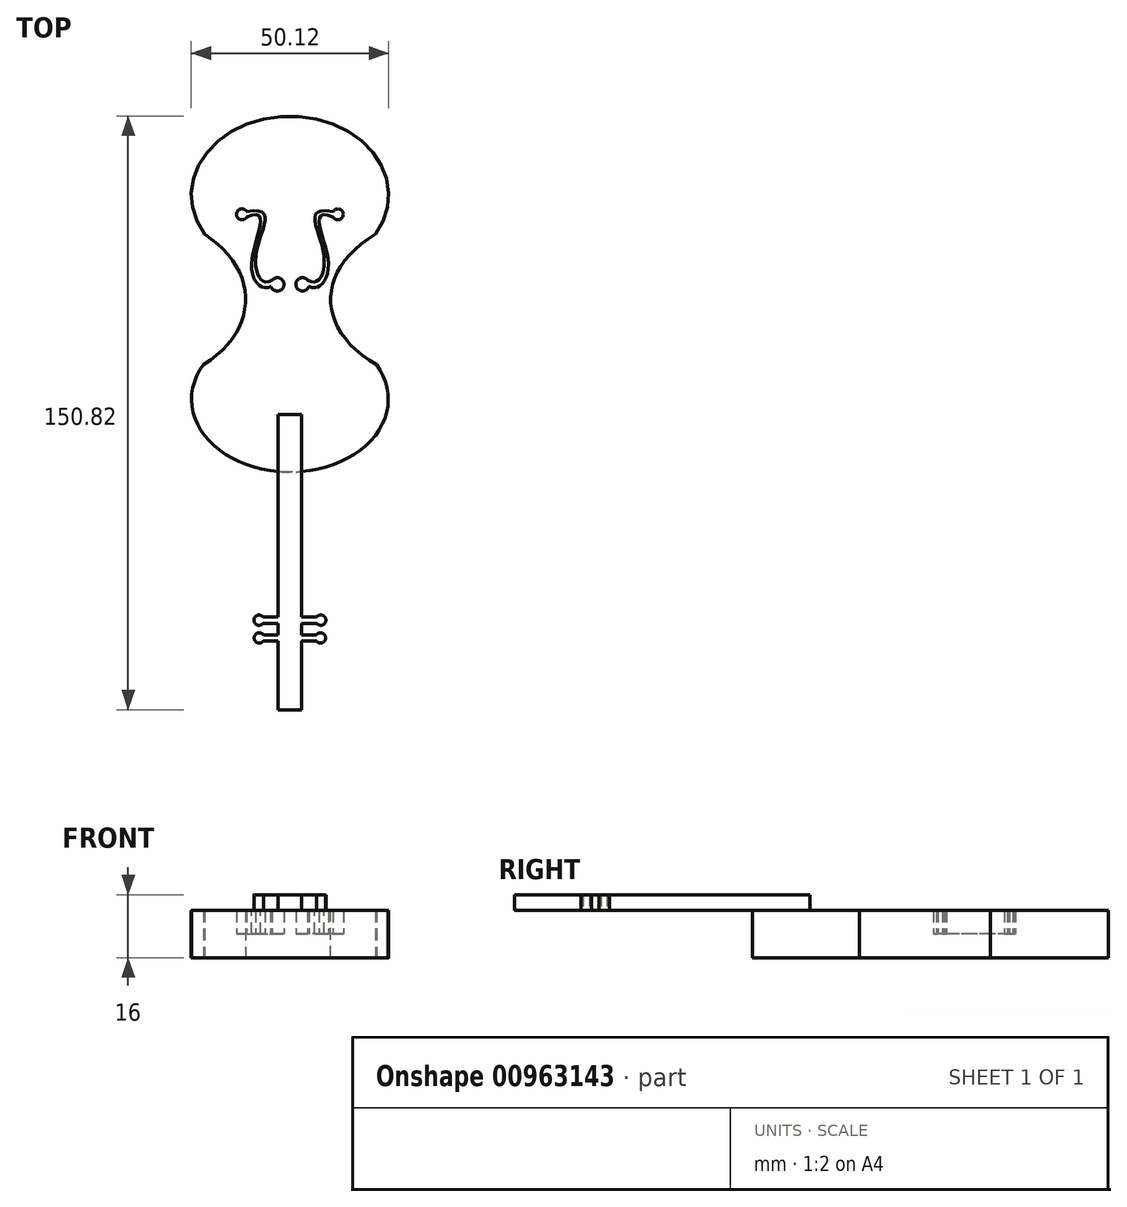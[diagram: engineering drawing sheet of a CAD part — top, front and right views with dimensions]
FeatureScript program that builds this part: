
annotation { "Feature Type Name" : "Feature", "Feature Type Description" : "" }
export const myFeature = defineFeature(function(context is Context, id is Id, definition is map)
    precondition{}
    {
        {
            var Q0;
            Q0=qCreatedBy(makeId("Top.planeOp"),FACE);
            var sketch = newSketch(context, id + "F0", { "sketchPlane" : qUnion([Q0])});
            skEllipticalArc(sketch, "E0", {});
            skEllipticalArc(sketch, "E1", {});
            skFitSpline(sketch, "E2", {"points": [v(21.74, 18.23) * mm, v(21.98, -14.95) * mm], "startDerivative": vector(-46.01, -28.19) * mm, "endDerivative": vector(46.18, -27.1) * mm});
            skFitSpline(sketch, "E3", {"points": [v(-21.74, 18.23) * mm, v(-21.98, -14.95) * mm], "startDerivative": vector(42.04, -27.25) * mm, "endDerivative": vector(-42.74, -26.33) * mm});
            const initialGuessF0  = {"E0": [0, -0.023745077083508568, 1, 0, 0.024989771066984055, 0.018479709246510986, 2.6455513247437614, 0.49604132884603214], "E1": [0, 0.02818056562631233, 1, 0, 0.025062327598065877, 0.020010533803968472, 5.762777835649319, 3.662000125120059]};
            skSetInitialGuess(sketch, initialGuessF0);
            skSolve(sketch);
        }
        {
            var Q0;
            Q0=makeQuery(id+"F0.imprint","IMPRINT",FACE,{"disambiguationData":[TD([[makeQuery(id+"F0.imprint","IMPRINT",EDGE,{"derivedFrom":sQuery(id+"F0.wireOp",EDGE,"E0")}),1.0]])]});
            extrude(context, id + "F1", {"entities" : qUnion([Q0]), "depth" : 6 * mm, "offsetDistance" : 25 * mm});
        }
        {
            var Q0;
            Q0=makeQuery(id+"F1.opExtrude","CAP_FACE",FACE,{"disambiguationData":[OSD([sQuery(id+"F0.wireOp",EDGE,"E0"),sQuery(id+"F0.wireOp",EDGE,"E1"),sQuery(id+"F0.wireOp",EDGE,"E2"),sQuery(id+"F0.wireOp",EDGE,"E3")])],"isStart":false});
            var sketch = newSketch(context, id + "F2", { "sketchPlane" : qUnion([Q0])});
            skFitSpline(sketch, "E4", {"points": [v(11, 22.54) * mm, v(9.71, 11.44) * mm, v(4.89, 4.9) * mm], "startDerivative": vector(-37.85, 16.1) * mm, "endDerivative": vector(-16.65, 8.43) * mm});
            skFitSpline(sketch, "E5.MirrorCS", {"points": [v(-11, 22.54) * mm, v(-9.71, 11.44) * mm, v(-4.89, 4.9) * mm], "startDerivative": vector(37.85, 16.1) * mm, "endDerivative": vector(16.65, 8.43) * mm});
            skFitSpline(sketch, "E6.MirrorCS", {"points": [v(-10.97, 23.93) * mm, v(-8.45, 14.05) * mm, v(-4.5, 6.53) * mm], "startDerivative": vector(45.34, 8.68) * mm, "endDerivative": vector(20.46, 12.4) * mm});
            skCircle(sketch, "E7", {"center": v(-12.18, 23.26) * mm, "radius": 1.39 * mm});
            skCircle(sketch, "E8", {"center": v(-3.2, 5.46) * mm, "radius": 1.69 * mm});
            skCircle(sketch, "E9.MirrorC", {"center": v(12.18, 23.26) * mm, "radius": 1.39 * mm});
            skCircle(sketch, "E10.MirrorC", {"center": v(3.2, 5.46) * mm, "radius": 1.69 * mm});
            skFitSpline(sketch, "E11.MirrorCS", {"points": [v(10.97, 23.93) * mm, v(8.45, 14.05) * mm, v(4.5, 6.53) * mm], "startDerivative": vector(-45.34, 8.68) * mm, "endDerivative": vector(-20.46, 12.4) * mm});
            skLineSegment(sketch, "E12", {"start": v(-4.89, 4.9) * mm, "end": v(-4.8, 4.9) * mm});
            skLineSegment(sketch, "E13", {"start": v(4.89, 4.9) * mm, "end": v(4.8, 4.9) * mm});
            skSolve(sketch);
        }
        {
            var Q0;
            {var subQ4=sQuery(id+"F2.wireOp",EDGE,"E4");Q0=makeQuery(id+"F2.imprint","IMPRINT",FACE,{"disambiguationData":[TD([[makeQuery(id+"F2.imprint","IMPRINT",EDGE,{"derivedFrom":subQ4}),1.0]])]});}
            extrude(context, id + "F3", {"entities" : qUnion([Q0]), "operationType" : NewBodyOperationType.ADD, "depth" : 6 * mm, "offsetDistance" : 25 * mm});
        }
        {
            var Q0;
            Q0=makeQuery(id+"F3.opExtrude","CAP_FACE",FACE,{"disambiguationData":[OSD([sQuery(id+"F0.wireOp",EDGE,"E0"),sQuery(id+"F0.wireOp",EDGE,"E1"),sQuery(id+"F0.wireOp",EDGE,"E2"),sQuery(id+"F0.wireOp",EDGE,"E3"),sQuery(id+"F2.wireOp",EDGE,"E4"),sQuery(id+"F2.wireOp",EDGE,"E5.MirrorCS"),sQuery(id+"F2.wireOp",EDGE,"E6.MirrorCS"),sQuery(id+"F2.wireOp",EDGE,"E7"),sQuery(id+"F2.wireOp",EDGE,"E8"),sQuery(id+"F2.wireOp",EDGE,"E9.MirrorC"),sQuery(id+"F2.wireOp",EDGE,"E10.MirrorC"),sQuery(id+"F2.wireOp",EDGE,"E11.MirrorCS"),sQuery(id+"F2.wireOp",EDGE,"E12"),sQuery(id+"F2.wireOp",EDGE,"E13")])],"isStart":false});
            var sketch = newSketch(context, id + "F4", { "sketchPlane" : qUnion([Q0])});
            skLineSegment(sketch, "E14.bottom", {"start": v(0, -27.63) * mm, "end": v(3, -27.63) * mm});
            skLineSegment(sketch, "E14.top", {"start": v(0, -102.63) * mm, "end": v(3, -102.63) * mm});
            skLineSegment(sketch, "E14.left", {"start": v(0, -27.63) * mm, "end": v(0, -102.63) * mm});
            skLineSegment(sketch, "E15.top", {"start": v(1.26, -27.63) * mm, "end": v(1.5, -27.63) * mm});
            skLineSegment(sketch, "E16.MirrorCS", {"start": v(-1.26, -27.63) * mm, "end": v(-1.5, -27.63) * mm});
            skLineSegment(sketch, "E17.MirrorCS", {"start": v(0, -27.63) * mm, "end": v(-3, -27.63) * mm});
            skLineSegment(sketch, "E18.MirrorCS", {"start": v(0, -102.63) * mm, "end": v(-3, -102.63) * mm});
            skLineSegment(sketch, "E19", {"start": v(-3, -27.63) * mm, "end": v(-3, -102.63) * mm});
            skLineSegment(sketch, "E20", {"start": v(3, -27.63) * mm, "end": v(3, -102.63) * mm});
            skLineSegment(sketch, "E21.bottom", {"start": v(3, -79.08) * mm, "end": v(7.13, -79.08) * mm});
            skLineSegment(sketch, "E21.top", {"start": v(3, -80.67) * mm, "end": v(7.13, -80.67) * mm});
            skLineSegment(sketch, "E21.left", {"start": v(3, -79.08) * mm, "end": v(3, -80.67) * mm});
            skLineSegment(sketch, "E21.right", {"start": v(7.13, -79.08) * mm, "end": v(7.13, -80.67) * mm});
            skCircle(sketch, "E22", {"center": v(7.83, -79.87) * mm, "radius": 1.3 * mm});
            skPoint(sketch, "E22.centerSnap0", {"position": v(7.13, -79.87) * mm});
            skLineSegment(sketch, "E23.bottom", {"start": v(3, -83.58) * mm, "end": v(7.08, -83.58) * mm});
            skLineSegment(sketch, "E23.top", {"start": v(3, -85.17) * mm, "end": v(7.08, -85.17) * mm});
            skLineSegment(sketch, "E23.right", {"start": v(7.08, -83.58) * mm, "end": v(7.08, -85.17) * mm});
            skCircle(sketch, "E24", {"center": v(7.78, -84.38) * mm, "radius": 1.3 * mm});
            skPoint(sketch, "E24.centerSnap0", {"position": v(7.08, -84.38) * mm});
            skLineSegment(sketch, "E25.MirrorCS", {"start": v(-3, -83.58) * mm, "end": v(-7.08, -83.58) * mm});
            skPoint(sketch, "E26.MirrorP", {"position": v(-7.08, -84.38) * mm});
            skLineSegment(sketch, "E27.MirrorCS", {"start": v(-7.08, -83.58) * mm, "end": v(-7.08, -85.17) * mm});
            skCircle(sketch, "E28.MirrorC", {"center": v(-7.78, -84.38) * mm, "radius": 1.3 * mm});
            skLineSegment(sketch, "E29.MirrorCS", {"start": v(-3, -85.17) * mm, "end": v(-7.08, -85.17) * mm});
            skLineSegment(sketch, "E30.MirrorCS", {"start": v(-3, -80.67) * mm, "end": v(-7.13, -80.67) * mm});
            skLineSegment(sketch, "E31.MirrorCS", {"start": v(-3, -79.08) * mm, "end": v(-7.13, -79.08) * mm});
            skLineSegment(sketch, "E32.MirrorCS", {"start": v(-7.13, -79.08) * mm, "end": v(-7.13, -80.67) * mm});
            skCircle(sketch, "E33.MirrorC", {"center": v(-7.83, -79.87) * mm, "radius": 1.3 * mm});
            skSolve(sketch);
        }
        {
            var Q0;
            {var subQ1=sQuery(id+"F4.wireOp",EDGE,"E14.bottom");var subQ5=makeQuery(id+"F4.imprint","IMPRINT",VERTEX,{"disambiguationData":[OD(0.0)],"derivedFrom":subQ1});Q0=makeQuery(id+"F4.imprint","IMPRINT",FACE,{"disambiguationData":[TD([[makeQuery(id+"F4.imprint","IMPRINT",EDGE,{"disambiguationData":[TD([[subQ5,1.0]])],"derivedFrom":subQ1}),-1.0]])]});}
            var Q1;
            {var subQ3=sQuery(id+"F4.wireOp",EDGE,"E16.MirrorCS");Q1=makeQuery(id+"F4.imprint","IMPRINT",FACE,{"disambiguationData":[TD([[makeQuery(id+"F4.imprint","IMPRINT",EDGE,{"derivedFrom":subQ3}),1.0]])]});}
            var Q2;
            {var subQ1=sQuery(id+"F4.wireOp",EDGE,"E18.MirrorCS");Q2=makeQuery(id+"F4.imprint","IMPRINT",FACE,{"disambiguationData":[TD([[makeQuery(id+"F4.imprint","IMPRINT",EDGE,{"derivedFrom":subQ1}),-1.0]])]});}
            var Q3;
            {var subQ5=sQuery(id+"F4.wireOp",EDGE,"E14.top");Q3=makeQuery(id+"F4.imprint","IMPRINT",FACE,{"disambiguationData":[TD([[makeQuery(id+"F4.imprint","IMPRINT",EDGE,{"derivedFrom":subQ5}),1.0]])]});}
            extrude(context, id + "F5", {"entities" : qUnion([Q0, Q1, Q2, Q3]), "operationType" : NewBodyOperationType.ADD, "depth" : 4 * mm, "offsetDistance" : 25 * mm});
        }
        {
            var Q0;
            {var subQ0=sQuery(id+"F4.wireOp",EDGE,"E21.right");var subQ1=sQuery(id+"F4.wireOp",EDGE,"E21.bottom");var subQ8=makeQuery(id+"F4.imprint","IMPRINT",EDGE,{"derivedFrom":subQ0});var subQ9=sQuery(id+"F4.wireOp",EDGE,"E19");var subQ10=sQuery(id+"F4.wireOp",EDGE,"E18.MirrorCS");var subQ11=sQuery(id+"F4.wireOp",EDGE,"E29.MirrorCS");var subQ12=makeQuery(id+"F4.imprint","INTERSECT",VERTEX,{"derivedFrom":[subQ9,subQ11]});var subQ18=sQuery(id+"F4.wireOp",EDGE,"E14.top");var subQ23=sQuery(id+"F4.wireOp",EDGE,"E30.MirrorCS");var subQ24=makeQuery(id+"F4.imprint","INTERSECT",VERTEX,{"derivedFrom":[subQ9,subQ23]});var subQ25=makeQuery(id+"F4.imprint","IMPRINT",EDGE,{"disambiguationData":[TD([[subQ24,1.0]])],"derivedFrom":subQ9});var subQ26=makeQuery(id+"F4.imprint","IMPRINT",EDGE,{"disambiguationData":[TD([[subQ12,1.0]])],"derivedFrom":subQ9});var subQ32=sQuery(id+"F4.wireOp",EDGE,"E27.MirrorCS");var subQ38=makeQuery(id+"F4.imprint","IMPRINT",EDGE,{"derivedFrom":subQ32});var subQ41=sQuery(id+"F4.wireOp",EDGE,"E14.bottom");var subQ44=makeQuery(id+"F4.imprint","IMPRINT",VERTEX,{"disambiguationData":[OD(0.0)],"derivedFrom":subQ41});var subQ46=sQuery(id+"F4.wireOp",EDGE,"E20");var subQ50=sQuery(id+"F4.wireOp",EDGE,"E23.right");var subQ55=sQuery(id+"F4.wireOp",EDGE,"E23.top");var subQ58=makeQuery(id+"F4.imprint","IMPRINT",EDGE,{"derivedFrom":subQ50});var subQ60=sQuery(id+"F4.wireOp",EDGE,"E32.MirrorCS");var subQ63=makeQuery(id+"F4.imprint","IMPRINT",EDGE,{"derivedFrom":subQ60});var subQ65=makeQuery(id+"F4.imprint","INTERSECT",VERTEX,{"derivedFrom":[subQ46,subQ55]});var subQ67=makeQuery(id+"F4.imprint","IMPRINT",EDGE,{"disambiguationData":[TD([[subQ65,1.0]])],"derivedFrom":subQ46});var subQ68=sQuery(id+"F4.wireOp",EDGE,"E16.MirrorCS");var subQ70=makeQuery(id+"F4.imprint","INTERSECT",VERTEX,{"derivedFrom":[subQ46,subQ1]});var subQ72=makeQuery(id+"F4.imprint","IMPRINT",EDGE,{"disambiguationData":[TD([[subQ70,-1.0]])],"derivedFrom":subQ46});Q0=qUnion([makeQuery(id+"F4.imprint","IMPRINT",FACE,{"disambiguationData":[TD([[subQ26,-1.0]])]}),makeQuery(id+"F4.imprint","IMPRINT",FACE,{"disambiguationData":[TD([[makeQuery(id+"F4.imprint","IMPRINT",EDGE,{"derivedFrom":subQ18}),1.0]])]}),makeQuery(id+"F4.imprint","IMPRINT",FACE,{"disambiguationData":[TD([[subQ58,1.0]])]}),makeQuery(id+"F4.imprint","IMPRINT",FACE,{"disambiguationData":[TD([[subQ72,1.0]])]}),makeQuery(id+"F4.imprint","IMPRINT",FACE,{"disambiguationData":[TD([[subQ38,-1.0]])]}),makeQuery(id+"F4.imprint","IMPRINT",FACE,{"disambiguationData":[TD([[makeQuery(id+"F4.imprint","IMPRINT",EDGE,{"derivedFrom":subQ68}),1.0]])]}),makeQuery(id+"F4.imprint","IMPRINT",FACE,{"disambiguationData":[TD([[subQ67,1.0]])]}),makeQuery(id+"F4.imprint","IMPRINT",FACE,{"disambiguationData":[TD([[subQ63,-1.0]])]}),makeQuery(id+"F4.imprint","IMPRINT",FACE,{"disambiguationData":[TD([[subQ8,-1.0]])]}),makeQuery(id+"F4.imprint","IMPRINT",FACE,{"disambiguationData":[TD([[subQ63,1.0]])]}),makeQuery(id+"F4.imprint","IMPRINT",FACE,{"disambiguationData":[TD([[subQ58,-1.0]])]}),makeQuery(id+"F4.imprint","IMPRINT",FACE,{"disambiguationData":[TD([[makeQuery(id+"F4.imprint","IMPRINT",EDGE,{"disambiguationData":[TD([[subQ44,1.0]])],"derivedFrom":subQ41}),-1.0]])]}),makeQuery(id+"F4.imprint","IMPRINT",FACE,{"disambiguationData":[TD([[subQ38,1.0]])]}),makeQuery(id+"F4.imprint","IMPRINT",FACE,{"disambiguationData":[TD([[subQ25,-1.0]])]}),makeQuery(id+"F4.imprint","IMPRINT",FACE,{"disambiguationData":[TD([[makeQuery(id+"F4.imprint","IMPRINT",EDGE,{"derivedFrom":subQ10}),-1.0]])]}),makeQuery(id+"F4.imprint","IMPRINT",FACE,{"disambiguationData":[TD([[subQ8,1.0]])]})]);}
            extrude(context, id + "F6", {"entities" : qUnion([Q0]), "operationType" : NewBodyOperationType.ADD, "depth" : 4 * mm, "offsetDistance" : 25 * mm});
        }
    });
